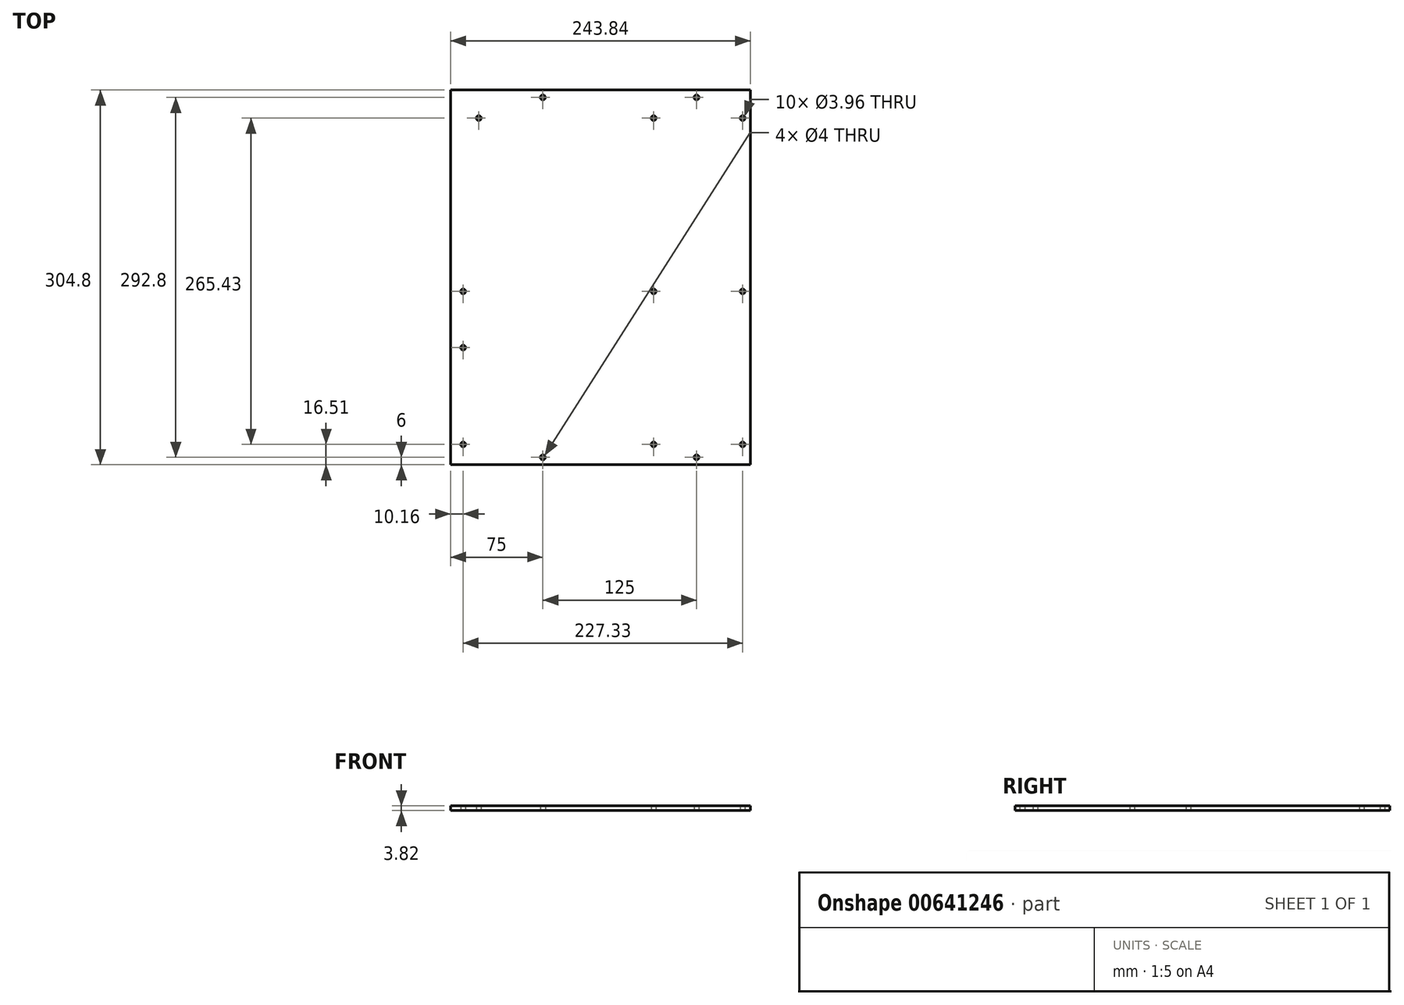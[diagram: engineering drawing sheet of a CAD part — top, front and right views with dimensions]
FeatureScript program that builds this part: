
annotation { "Feature Type Name" : "Feature", "Feature Type Description" : "" }
export const myFeature = defineFeature(function(context is Context, id is Id, definition is map)
    precondition{}
    {
        {
            var Q0;
            Q0=qCreatedBy(makeId("Top.planeOp"),FACE);
            var sketch = newSketch(context, id + "F0", { "sketchPlane" : qUnion([Q0])});
            skLineSegment(sketch, "E0.bottom", {"start": v(121.92, 152.4) * mm, "end": v(-121.92, 152.4) * mm});
            skLineSegment(sketch, "E0.top", {"start": v(121.92, -152.4) * mm, "end": v(-121.92, -152.4) * mm});
            skLineSegment(sketch, "E0.left", {"start": v(121.92, 152.4) * mm, "end": v(121.92, -152.4) * mm});
            skLineSegment(sketch, "E0.right", {"start": v(-121.92, 152.4) * mm, "end": v(-121.92, -152.4) * mm});
            skPoint(sketch, "E0.middle", {"position": v(0, 0) * mm});
            skPoint(sketch, "E1", {"position": v(-121.92, -152.4) * mm});
            skCircle(sketch, "E2", {"center": v(-99.06, 129.54) * mm, "radius": 1.98 * mm});
            skCircle(sketch, "E3", {"center": v(-111.76, -135.9) * mm, "radius": 1.98 * mm});
            skCircle(sketch, "E4", {"center": v(43.18, -135.9) * mm, "radius": 1.98 * mm});
            skCircle(sketch, "E5", {"center": v(115.57, -135.9) * mm, "radius": 1.98 * mm});
            skCircle(sketch, "E6", {"center": v(-111.76, -57.15) * mm, "radius": 1.98 * mm});
            skCircle(sketch, "E7", {"center": v(-111.76, -11.43) * mm, "radius": 1.98 * mm});
            skCircle(sketch, "E8", {"center": v(43.18, -11.43) * mm, "radius": 1.98 * mm});
            skCircle(sketch, "E9", {"center": v(115.57, -11.43) * mm, "radius": 1.98 * mm});
            skCircle(sketch, "E10", {"center": v(43.18, 129.54) * mm, "radius": 1.98 * mm});
            skCircle(sketch, "E11", {"center": v(115.57, 129.54) * mm, "radius": 1.98 * mm});
            skCircle(sketch, "E12", {"center": v(-46.92, -146.4) * mm, "radius": 2 * mm});
            skCircle(sketch, "E13", {"center": v(78.08, -146.4) * mm, "radius": 2 * mm});
            skCircle(sketch, "E14", {"center": v(-46.92, 146.4) * mm, "radius": 2 * mm});
            skCircle(sketch, "E15", {"center": v(78.08, 146.4) * mm, "radius": 2 * mm});
            skSolve(sketch);
        }
        {
            var Q0;
            Q0=makeQuery(id+"F0.imprint","IMPRINT",FACE,{"disambiguationData":[TD([[makeQuery(id+"F0.imprint","IMPRINT",EDGE,{"derivedFrom":sQuery(id+"F0.wireOp",EDGE,"E0.bottom")}),1.0]])]});
            extrude(context, id + "F1", {"entities" : qUnion([Q0]), "endBound" : BoundingType.SYMMETRIC, "depth" : 3.8 * mm, "offsetDistance" : 25.4 * mm});
        }
    });
